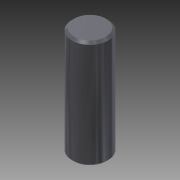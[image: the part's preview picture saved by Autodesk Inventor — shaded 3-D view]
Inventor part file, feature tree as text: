
AUTODESK INVENTOR PART (.ipt)
format: ipt  version: 2011 SP2 (Build 150309200, 309)  size: 77,824 bytes
history: native  units: mm
features: chamfer x2, extrude x1, sketch x1
ambient origin geometry x8: Origin, YZ Plane, XZ Plane, XY Plane, X Axis, Y Axis, Z Axis, Center Point
bodies: Solid1 (feature_tree)
feature tree (4):
  extrude  "Extrusion1"  Depth=48.0mm TaperAngle=0.0deg
  chamfer  "Chamfer1"  Distance=1.0mm Angle=45.0deg
  chamfer  "Chamfer2"  Distance=1.0mm Angle=45.0deg
  sketch  "Sketch1"  dims[d0=8.0mm d1=48.0mm d2=0.0mm d3=1.0mm d4=2.0mm d5=45.0deg d6=1.0mm d7=2.0mm d8=45.0deg]
